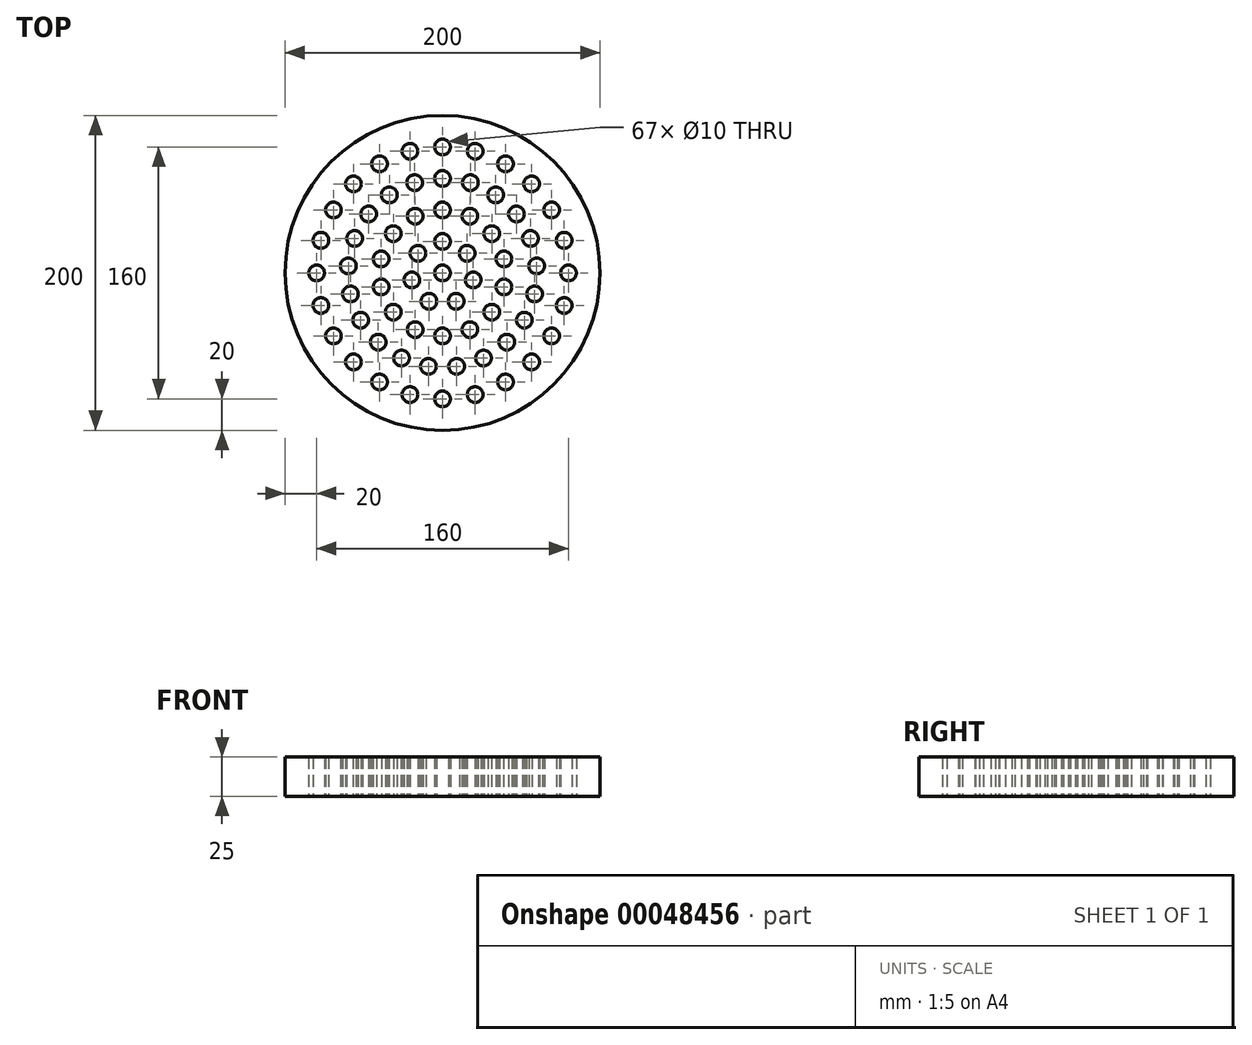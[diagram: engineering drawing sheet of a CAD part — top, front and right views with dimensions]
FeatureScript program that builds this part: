
annotation { "Feature Type Name" : "Feature", "Feature Type Description" : "" }
export const myFeature = defineFeature(function(context is Context, id is Id, definition is map)
    precondition{}
    {
        {
            var Q0;
            Q0=qCreatedBy(makeId("Top.planeOp"),FACE);
            var sketch = newSketch(context, id + "F0", { "sketchPlane" : qUnion([Q0])});
            skCircle(sketch, "E0", {"center": v(0, 0) * mm, "radius": 5 * mm});
            skCircle(sketch, "E1.0.1.0", {"center": v(0, 20) * mm, "radius": 5 * mm});
            skCircle(sketch, "E1.0.2.0", {"center": v(0, 40) * mm, "radius": 5 * mm});
            skCircle(sketch, "E1.0.3.0", {"center": v(0, 60) * mm, "radius": 5 * mm});
            skCircle(sketch, "E1.0.4.0", {"center": v(0, 80) * mm, "radius": 5 * mm});
            skLineSegment(sketch, "E1.direction1", {"start": v(0, 0) * mm, "end": v(25, 0) * mm, "construction": true});
            skLineSegment(sketch, "E1.direction2", {"start": v(0, 0) * mm, "end": v(0, 20) * mm, "construction": true});
            skCircle(sketch, "E2.1.0", {"center": v(-20.7, 77.27) * mm, "radius": 5 * mm});
            skCircle(sketch, "E2.2.0", {"center": v(-40, 69.28) * mm, "radius": 5 * mm});
            skCircle(sketch, "E2.3.0", {"center": v(-56.57, 56.57) * mm, "radius": 5 * mm});
            skCircle(sketch, "E2.4.0", {"center": v(-69.28, 40) * mm, "radius": 5 * mm});
            skCircle(sketch, "E2.5.0", {"center": v(-77.27, 20.7) * mm, "radius": 5 * mm});
            skCircle(sketch, "E2.6.0", {"center": v(-80, 0) * mm, "radius": 5 * mm});
            skCircle(sketch, "E2.7.0", {"center": v(-77.27, -20.7) * mm, "radius": 5 * mm});
            skCircle(sketch, "E2.8.0", {"center": v(-69.28, -40) * mm, "radius": 5 * mm});
            skCircle(sketch, "E2.9.0", {"center": v(-56.57, -56.57) * mm, "radius": 5 * mm});
            skCircle(sketch, "E2.10.0", {"center": v(-40, -69.28) * mm, "radius": 5 * mm});
            skCircle(sketch, "E2.11.0", {"center": v(-20.7, -77.27) * mm, "radius": 5 * mm});
            skCircle(sketch, "E2.12.0", {"center": v(0, -80) * mm, "radius": 5 * mm});
            skCircle(sketch, "E2.13.0", {"center": v(20.7, -77.27) * mm, "radius": 5 * mm});
            skCircle(sketch, "E2.14.0", {"center": v(40, -69.28) * mm, "radius": 5 * mm});
            skCircle(sketch, "E2.15.0", {"center": v(56.57, -56.57) * mm, "radius": 5 * mm});
            skCircle(sketch, "E2.16.0", {"center": v(69.28, -40) * mm, "radius": 5 * mm});
            skCircle(sketch, "E2.17.0", {"center": v(77.27, -20.7) * mm, "radius": 5 * mm});
            skCircle(sketch, "E2.18.0", {"center": v(80, 0) * mm, "radius": 5 * mm});
            skCircle(sketch, "E2.19.0", {"center": v(77.27, 20.7) * mm, "radius": 5 * mm});
            skCircle(sketch, "E2.20.0", {"center": v(69.28, 40) * mm, "radius": 5 * mm});
            skCircle(sketch, "E2.21.0", {"center": v(56.57, 56.57) * mm, "radius": 5 * mm});
            skCircle(sketch, "E2.22.0", {"center": v(40, 69.28) * mm, "radius": 5 * mm});
            skCircle(sketch, "E2.23.0", {"center": v(20.7, 77.27) * mm, "radius": 5 * mm});
            skCircle(sketch, "E3.1.0", {"center": v(-17.69, 57.33) * mm, "radius": 5 * mm});
            skCircle(sketch, "E3.2.0", {"center": v(-33.8, 49.57) * mm, "radius": 5 * mm});
            skCircle(sketch, "E3.3.0", {"center": v(-46.9, 37.4) * mm, "radius": 5 * mm});
            skCircle(sketch, "E3.4.0", {"center": v(-55.85, 21.92) * mm, "radius": 5 * mm});
            skCircle(sketch, "E3.5.0", {"center": v(-59.83, 4.48) * mm, "radius": 5 * mm});
            skCircle(sketch, "E3.6.0", {"center": v(-58.5, -13.35) * mm, "radius": 5 * mm});
            skCircle(sketch, "E3.7.0", {"center": v(-51.96, -30) * mm, "radius": 5 * mm});
            skCircle(sketch, "E3.8.0", {"center": v(-40.81, -43.98) * mm, "radius": 5 * mm});
            skCircle(sketch, "E3.9.0", {"center": v(-26.03, -54.06) * mm, "radius": 5 * mm});
            skCircle(sketch, "E3.10.0", {"center": v(-8.94, -59.33) * mm, "radius": 5 * mm});
            skCircle(sketch, "E3.11.0", {"center": v(8.94, -59.33) * mm, "radius": 5 * mm});
            skCircle(sketch, "E3.12.0", {"center": v(26.03, -54.06) * mm, "radius": 5 * mm});
            skCircle(sketch, "E3.13.0", {"center": v(40.81, -43.98) * mm, "radius": 5 * mm});
            skCircle(sketch, "E3.14.0", {"center": v(51.96, -30) * mm, "radius": 5 * mm});
            skCircle(sketch, "E3.15.0", {"center": v(58.5, -13.35) * mm, "radius": 5 * mm});
            skCircle(sketch, "E3.16.0", {"center": v(59.83, 4.48) * mm, "radius": 5 * mm});
            skCircle(sketch, "E3.17.0", {"center": v(55.85, 21.92) * mm, "radius": 5 * mm});
            skCircle(sketch, "E3.18.0", {"center": v(46.9, 37.4) * mm, "radius": 5 * mm});
            skCircle(sketch, "E3.19.0", {"center": v(33.8, 49.57) * mm, "radius": 5 * mm});
            skCircle(sketch, "E3.20.0", {"center": v(17.69, 57.33) * mm, "radius": 5 * mm});
            skCircle(sketch, "E4.1.0", {"center": v(-15.64, 12.47) * mm, "radius": 5 * mm});
            skCircle(sketch, "E4.2.0", {"center": v(-19.5, -4.45) * mm, "radius": 5 * mm});
            skCircle(sketch, "E4.3.0", {"center": v(-8.68, -18.02) * mm, "radius": 5 * mm});
            skCircle(sketch, "E4.4.0", {"center": v(8.68, -18.02) * mm, "radius": 5 * mm});
            skCircle(sketch, "E4.5.0", {"center": v(19.5, -4.45) * mm, "radius": 5 * mm});
            skCircle(sketch, "E4.6.0", {"center": v(15.64, 12.47) * mm, "radius": 5 * mm});
            skCircle(sketch, "E5.1.0", {"center": v(-17.36, 36.04) * mm, "radius": 5 * mm});
            skCircle(sketch, "E5.2.0", {"center": v(-31.27, 24.94) * mm, "radius": 5 * mm});
            skCircle(sketch, "E5.3.0", {"center": v(-39, 8.9) * mm, "radius": 5 * mm});
            skCircle(sketch, "E5.4.0", {"center": v(-39, -8.9) * mm, "radius": 5 * mm});
            skCircle(sketch, "E5.5.0", {"center": v(-31.27, -24.94) * mm, "radius": 5 * mm});
            skCircle(sketch, "E5.6.0", {"center": v(-17.36, -36.04) * mm, "radius": 5 * mm});
            skCircle(sketch, "E5.7.0", {"center": v(0, -40) * mm, "radius": 5 * mm});
            skCircle(sketch, "E5.8.0", {"center": v(17.36, -36.04) * mm, "radius": 5 * mm});
            skCircle(sketch, "E5.9.0", {"center": v(31.27, -24.94) * mm, "radius": 5 * mm});
            skCircle(sketch, "E5.10.0", {"center": v(39, -8.9) * mm, "radius": 5 * mm});
            skCircle(sketch, "E5.11.0", {"center": v(39, 8.9) * mm, "radius": 5 * mm});
            skCircle(sketch, "E5.12.0", {"center": v(31.27, 24.94) * mm, "radius": 5 * mm});
            skCircle(sketch, "E5.13.0", {"center": v(17.36, 36.04) * mm, "radius": 5 * mm});
            skSolve(sketch);
        }
        {
            var Q0;
            Q0=qCreatedBy(makeId("Top.planeOp"),FACE);
            var sketch = newSketch(context, id + "F1", { "sketchPlane" : qUnion([Q0])});
            skCircle(sketch, "E6", {"center": v(0, 0) * mm, "radius": 100 * mm});
            skSolve(sketch);
        }
        {
            var Q0;
            Q0=makeQuery(id+"F1.imprint","IMPRINT",FACE,{"disambiguationData":[TD([[makeQuery(id+"F1.imprint","IMPRINT",EDGE,{"derivedFrom":sQuery(id+"F1.wireOp",EDGE,"E6")}),1.0]])]});
            extrude(context, id + "F2", {"entities" : qUnion([Q0]), "depth" : 25 * mm});
        }
        {
            var Q0;
            Q0 = qSketchRegion(id + "F0", true);
            extrude(context, id + "F3", {"entities" : qUnion([Q0]), "operationType" : NewBodyOperationType.REMOVE, "endBound" : BoundingType.THROUGH_ALL, "depth" : 25 * mm});
        }
    });
